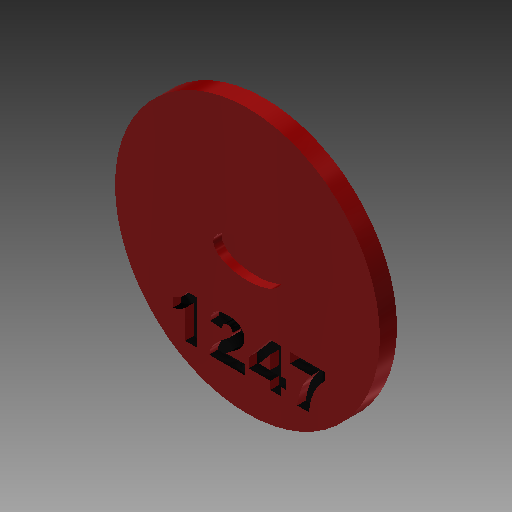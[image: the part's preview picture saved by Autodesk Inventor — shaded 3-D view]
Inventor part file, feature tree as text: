
AUTODESK INVENTOR PART (.ipt)
format: ipt  version: 2017 (Build 210142000, 142)  size: 594,432 bytes
history: native  units: in
note: dims shown in document units (in); Inventor stores cm internally (conversion verified against a paired STEP export)
features: sketch x24, extrude x18, plane x9, projected_geometry x5, loft x4, other x3, mirror x1, emboss x1, fillet x1, reference x1
ambient origin geometry x8: Origin, YZ Plane, XZ Plane, XY Plane, X Axis, Y Axis, Z Axis, Center Point
bodies: Solid1 (feature_tree)
feature tree (67):
  sketch  "Sketch1"  dims[d0=0.7559in d1=0.7559in]
  plane  "Work Plane1"
  loft  "Loft1"
  extrude  "Extrusion1"  Depth=0.2in
  plane  "Work Plane4"
  loft  "Loft2"
  plane  "Work Plane5"
  loft  "Loft3"
  loft  "Loft4"
  extrude  "Extrusion2"  TaperAngle=0.0deg  [1 undecoded]
  plane  "Work Plane6"
  extrude  "Extrusion3"  Depth=1.0in
  extrude  "Extrusion4"  Depth=1.0651in
  extrude  "Extrusion5"  Depth=0.962in
  plane  "Work Plane7"
  extrude  "Extrusion6"  Depth=0.075in
  plane  "Work Plane8"
  other  "Work Axis1"
  plane  "Work Plane9"
  extrude  "Extrusion7"  Depth=0.06in
  mirror  "Mirror3"
  extrude  "Extrusion8"  Depth=0.05in
  plane  "Work Plane10"
  extrude  "Extrusion9"  Depth=0.0625in
  plane  "Work Plane11"
  extrude  "Extrusion10"  Depth=0.075in
  extrude  "Extrusion11"  TaperAngle=0.0deg  [1 undecoded]
  extrude  "Extrusion12"  Depth=0.2in
  extrude  "Extrusion13"  TaperAngle=0.0deg  [1 undecoded]
  emboss  "Emboss1"
  extrude  "Extrusion16"  Depth=0.01in
  extrude  "Extrusion17"  Depth=0.0344in
  extrude  "Extrusion18"  TaperAngle=60.0deg  [1 undecoded]
  fillet  "Fillet1"  [1 undecoded]
  extrude  "Extrusion20"  Depth=0.05in
  extrude  "Extrusion21"  Depth=0.05in
  sketch  "Sketch2"  dims[d2=0.9963in d3=0.2in]
  sketch  "Sketch3"  dims[d4=0.5in d6=0.08in]
  sketch  "Sketch4"  dims[d7=0.55in d8=150.0deg]
  other  "Edges1"
  sketch  "Sketch5"  dims[d9=150.0deg d14=0.33in]
  projected_geometry  "Projected Loop1"
  other  "Edges2"
  sketch  "Sketch6"  dims[d15=0.66in d18=0.0in d19=90.0deg]
  sketch  "Sketch7"  dims[d20=0.0in d21=90.0deg d22=1.0in]
  sketch  "Sketch8"  dims[d26=1.0651in d28=1.0651in]
  sketch  "Sketch9"  dims[d29=0.0in d30=0.962in]
  sketch  "Sketch10"  dims[d31=0.962in d32=0.075in]
  sketch  "Sketch11"  dims[d33=0.15in d34=0.06in]
  sketch  "Sketch12"  dims[d35=0.1in d36=0.05in]
  sketch  "Sketch13"  dims[d37=0.45in d38=0.0in d39=0.0625in]
  projected_geometry  "Projected Loop2"
  projected_geometry  "Projected Loop3"
  sketch  "Sketch14"  dims[d40=0.01in d41=0.075in]
  projected_geometry  "Projected Loop4"
  sketch  "Sketch15"  dims[d42=0.01in d43=0.0in d44=90.0deg]
  sketch  "Sketch16"  dims[d45=0.0in d46=90.0deg d47=0.2in]
  sketch  "Sketch17"  dims[d48=0.07in d49=0.0in d50=90.0deg]
  sketch  "Sketch18"  dims[d51=0.0in d52=90.0deg d53=0.01in]
  sketch  "Sketch19"  dims[d54=0.01in d55=0.0344in]
  sketch  "Sketch23"  dims[d56=150.0deg d57=60.0deg d58=150.0deg]
  projected_geometry  "Projected Loop6"
  sketch  "Sketch24"  dims[d59=0.7in d60=0.05in]
  sketch  "Sketch25"  dims[d61=0.05in d62=0.05in d63=0.05in]
  sketch  "Sketch27"  dims[d64=0.05in]
  sketch  "Sketch28"  dims[d65=0.01in d66=0.0in d67=90.0deg d68=0.0in d69=90.0deg d70=0.1in d71=0.4in d72=0.15in d73=0.05in d74=0.0in d75=0.02in d77=0.15in d78=0.02in d79=0.1in d80=0.1in d81=0.1in d82=0.02in d83=0.15in d84=0.05in d85=0.0in d86=0.045in d87=0.0in d88=0.025in d89=0.0in d90=0.02in d91=0.02in d92=0.005in d93=0.0in d94=90.0deg d95=0.4466in d96=1.0in d97=0.0in d98=1.0in d99=0.0in d100=0.6528in d101=0.0in d102=0.0in d103=1.0in d104=0.0in d106=90.0deg d107=1.0in d108=0.0in d109=1.65in d110=0.1in d111=0.1in d112=0.0in d113=0.1in d114=0.075in d115=0.0in d116=0.05in d117=0.0in d123=0.84in d124=0.8in d125=0.0in d126=0.0in d127=1.0in d128=0.0in d130=0.15in d131=-0.0206in d135=0.2in d136=0.05in d137=0.1in d140=0.05in d141=0.1in d142=0.0in d143=0.0999in d144=0.2in d145=0.05in d146=0.0in]
  reference  "Reference1"
note: 5 required parameter values undecoded (feature->parameter linkage not recoverable at this tier; creation-order binding heuristic only, values carry confidence <= 0.55)
